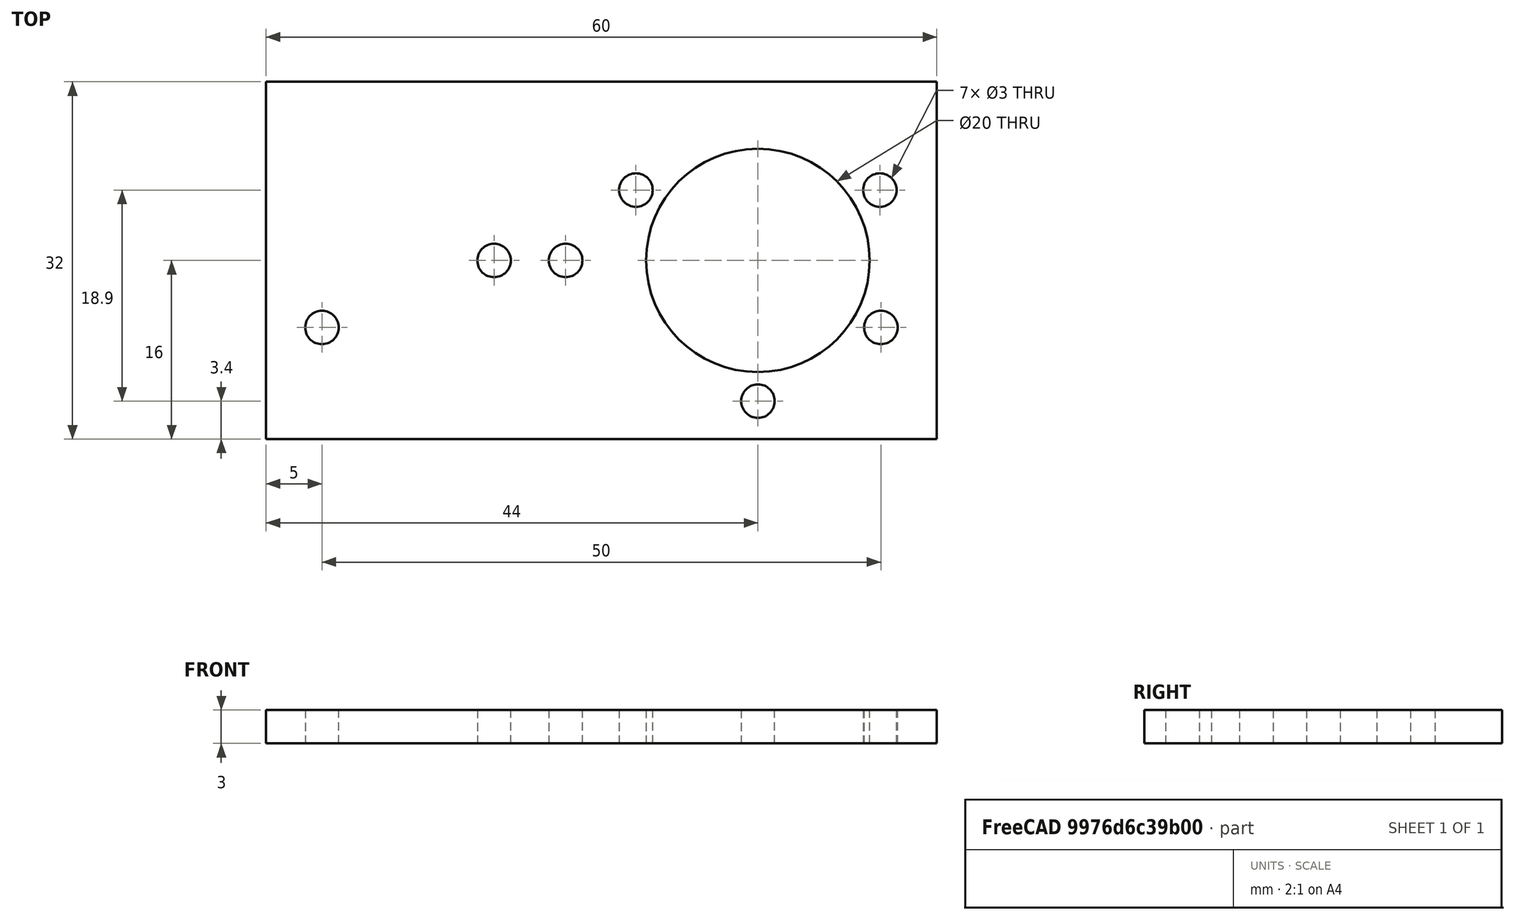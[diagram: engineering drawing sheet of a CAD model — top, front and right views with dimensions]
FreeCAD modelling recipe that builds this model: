
FCSTD DOCUMENT  (FreeCAD 0.16R6707 (Git))
Label: support_bas
License: All rights reserved
LicenseURL: http://en.wikipedia.org/wiki/All_rights_reserved
objects: Sketcher::SketchObject×1, PartDesign::Pad×1
note: 3 computed .brp shape members not serialized (recipe doc carries the construction recipe); baked Part::Feature solids carry a one-line shape summary decoded from their .brp

FEATURE [Sketcher::SketchObject] Sketch
  sketch-geometry (21):
    g0: LineSegment StartX=0 StartY=0 StartZ=0 EndX=60 EndY=0 EndZ=0
    g1: LineSegment StartX=60 StartY=0 StartZ=0 EndX=60 EndY=32 EndZ=0
    g2: LineSegment StartX=60 StartY=32 StartZ=0 EndX=0 EndY=32 EndZ=0
    g3: LineSegment StartX=0 StartY=32 StartZ=0 EndX=0 EndY=0 EndZ=0
    g4: GeomPoint [constr] X=44 Y=16 Z=0
    g5: GeomPoint [constr] X=55 Y=10 Z=0
    g6: GeomPoint [constr] X=44 Y=3.4 Z=0
    g7: GeomPoint [constr] X=54.9119 Y=22.3 Z=0
    g8: GeomPoint [constr] X=33.0881 Y=22.3 Z=0
    g9: Circle CenterX=33.0881 CenterY=22.3 CenterZ=0 NormalX=0 NormalY=0 NormalZ=1 Radius=1.5
    g10: Circle CenterX=54.9119 CenterY=22.3 CenterZ=0 NormalX=0 NormalY=0 NormalZ=1 Radius=1.5
    g11: Circle CenterX=44 CenterY=3.4 CenterZ=0 NormalX=0 NormalY=0 NormalZ=1 Radius=1.5
    g12: Circle CenterX=55 CenterY=10 CenterZ=0 NormalX=0 NormalY=0 NormalZ=1 Radius=1.5
    g13: GeomPoint [constr] X=5 Y=10 Z=0
    g14: Circle CenterX=5 CenterY=10 CenterZ=0 NormalX=0 NormalY=0 NormalZ=1 Radius=1.5
    g15: Circle CenterX=44 CenterY=16 CenterZ=0 NormalX=0 NormalY=0 NormalZ=1 Radius=10
    g16: Circle CenterX=20.4 CenterY=16 CenterZ=0 NormalX=0 NormalY=0 NormalZ=1 Radius=1.5
    g17: Circle CenterX=26.8 CenterY=16 CenterZ=0 NormalX=0 NormalY=0 NormalZ=1 Radius=1.5
    g18: GeomPoint [constr] X=46 Y=16 Z=0
    g19: GeomPoint [constr] X=39.6 Y=16 Z=0
    g20: GeomPoint [constr] X=33.2 Y=16 Z=0
  constraints (41):
    c: Coincident(g0,g1)
    c: Coincident(g1,g2)
    c: Coincident(g2,g3)
    c: Coincident(g3,g0)
    c: Horizontal(g0)
    c: Horizontal(g2)
    c: Vertical(g1)
    c: Vertical(g3)
    c: Coincident(g0,g-1)
    c: Distance(g3) = 32
    c: Distance(g2) = 60
    c: DistanceY(g4) = 16
    c: DistanceX(g4,g0) = 16
    c: DistanceX(g5,g0) = 5
    c: DistanceY(g5) = 10
    c: Coincident(g9,g8)
    c: Coincident(g10,g7)
    c: Coincident(g11,g6)
    c: Radius(g10) = 1.5
    c: Equal(g10,g9)
    c: Equal(g10,g11)
    c: Coincident(g12,g5)
    c: DistanceY(g13) = 10
    c: DistanceX(g13) = 5
    c: Coincident(g14,g13)
    c: Radius(g14) = 1.5
    c: Equal(g14,g12)
    c: Coincident(g15,g4)
    c: Radius(g15) = 10
    c: DistanceY(g17,g16) = 0
    c: DistanceX(g16,g17) = 6.4
    c: DistanceX(g18,g0) = 14
    c: DistanceY(g0,g18) = 16
    c: DistanceX(g19,g18) = 6.4
    c: DistanceX(g20,g19) = 6.4
    c: DistanceY(g19,g20) = 0
    c: DistanceY(g18,g19) = 0
    c: DistanceY(g20,g17) = 0
    c: DistanceX(g17,g20) = 6.4
    c: Radius(g16) = 1.5
    c: Equal(g16,g17)
FEATURE [PartDesign::Pad] Pad
  Length = 3
  Length2 = 100
  Sketch = -> Sketch
  Type = 0
